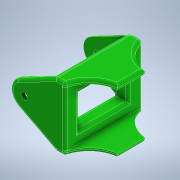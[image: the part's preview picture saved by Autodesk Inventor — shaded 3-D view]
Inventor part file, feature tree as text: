
AUTODESK INVENTOR PART (.ipt)
format: ipt  version: 2022 (Build 260153000, 153)  size: 240,640 bytes
history: native  units: in
note: dims shown in document units (in); Inventor stores cm internally (conversion verified against a paired STEP export)
features: sketch x4, extrude x3, fillet x1
ambient origin geometry x8: Origin, YZ Plane, XZ Plane, XY Plane, X Axis, Y Axis, Z Axis, Center Point
bodies: Solid1 (feature_tree)
feature tree (8):
  sketch  "Sketch1"  dims[d1=2.5591in d2=0.1969in d3=1.811in]
  extrude  "Extrusion1"  Depth=1.811in
  extrude  "Extrusion2"  Depth=0.7874in
  extrude  "Extrusion3"  Depth=0.7087in
  fillet  "Fillet1"  Radius=2.2047in
  sketch  "Sketch2"  dims[d5=0.1181in d6=0.7874in]
  sketch  "Sketch3"  dims[d7=2.2047in d8=0.0in d9=0.7087in d11=2.2047in d12=0.0in]
  sketch  "Sketch4"  dims[d13=2.2047in d14=0.0in d15=0.0787in]
